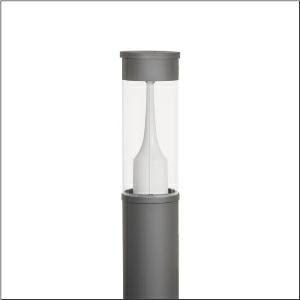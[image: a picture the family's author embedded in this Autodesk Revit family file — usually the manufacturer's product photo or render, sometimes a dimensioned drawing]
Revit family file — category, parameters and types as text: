
# Revit family: city-light_260_iq___p1_0a_5xa5295ff14h_c360
name_source: partatom
category: Lighting Fixtures
units: mm (PartAtom-declared; Revit-internal decimal feet)

## family parameters
Cut with Voids When Loaded = No
Host = Face
Light Source = No
Part Type = Normal
Room Calculation Point = No
Round Connector Dimension = Use Diameter
Shared = No

## types (1)
- --- (1 x LED, 1510 lm, 10.5 W, 3000K)
    Apparent Load = 11 VA
    CIE Flux Codes = 32 61 90 93 100
    Color Rendering = 70
    Color Temperature = 3000K
    Default Elevation = 1800 mm
    Description = City-Light 260 iQ, light pillar, Module 540 iQ-SR, primary light control with 3 zone facetted reflector, of plastic, silver coated, highly specular, structured, primary optical cover: cover, of PMMA, transparent, light distribution: P1.0a, primary light characteristic: strongly asymmetric, LED, High Power LED, rated luminous flux: 1.510lm, luminous efficacy: 144lm/W, light colour: 730, colour temperature: 3000K, control gear: ECG iQ, control: Auto-Match, Temp-Guard, Lumen-Switch, Night-Set, Smart-Wire, Light-Fading, Desk-Remote (wireless, voltage-free reading and setting of iQ features in the workshop via application-optimized NFC function/RFID function), optimised constant luminous flux control (CLO 2.0), Street-Remote, presetting dimming logarithmic, with terminal, 6-pole, max. 2.5mm², mains connection: 230..240V, AC, 50/60Hz, start of lifetime: 11W, end of service life: 11W, reduction: 5W, luminaire housing, cylindrical, of extruded aluminium section, coated, Siteco® metallic grey (DB 702S), length: 2.600mm, diameter: 200mm, Module 540 iQ-SR, traffic white (RAL 9016), equipment: standard, protection rating (complete): IP65, insulation class (complete): insulation class II (safety insulation), certification: CE, ENEC, VDE, packaging unit: 1 piece

Light Distribution: P1.0a
    Height = 500 mm
    Lamp = 1 x LED
    Lamp Light Flux = 1510 lm
    Lamp Power = 10.5 W
    Lamp count = 1
    Length = 200 mm  [stored 0.656168 ft]
    Luminous efficacy = 144 lm/W
    Manufacturer = Siteco
    ModVariant = No
    Model = 5XA5295FF14H
    Mounting Place = Floor
    Mounting Type = Freestanding
    Number of Poles = 1
    OnlyDefault = Yes
    Power Factor = 1
    Product Name = City-Light 260 iQ | P1.0a
    Product group = light pillar
    ProductGroupID = 1303
    Protection Class = Protection class II
    Protection Degree = IP 65
    RLX_Detail_Level = 1
    RLX_Emergency_Light_Flux = 0 lm
    RLX_Emergency_Type = 0
    RLX_Emergency_Type_DB = No
    RlxData = <blob elided: 52425 chars, md5=16a108e7>
    Socket = socket
    Standby Power = 0 W
    System Light Flux = 1510 lm
    System Power = 11 W
    Type Comments = factory setting: luminous flux: 100 % | dim-lin: 254 | 419 mA
    Type Image = l_1006918.jpg
    URL = http://relux.com
    VarID = @adj_091821
    Voltage = 0 V
    Weight = 0.00 kg
    Width = 0 mm  [stored 0 ft]

note: [stored X ft] marks values corroborated as IEEE doubles in the binary element streams (Revit-internal decimal feet)

## geometry (parser evidence)
native form markers: Blend x4, Sweep x10
no freeform markers — native parametric forms only
